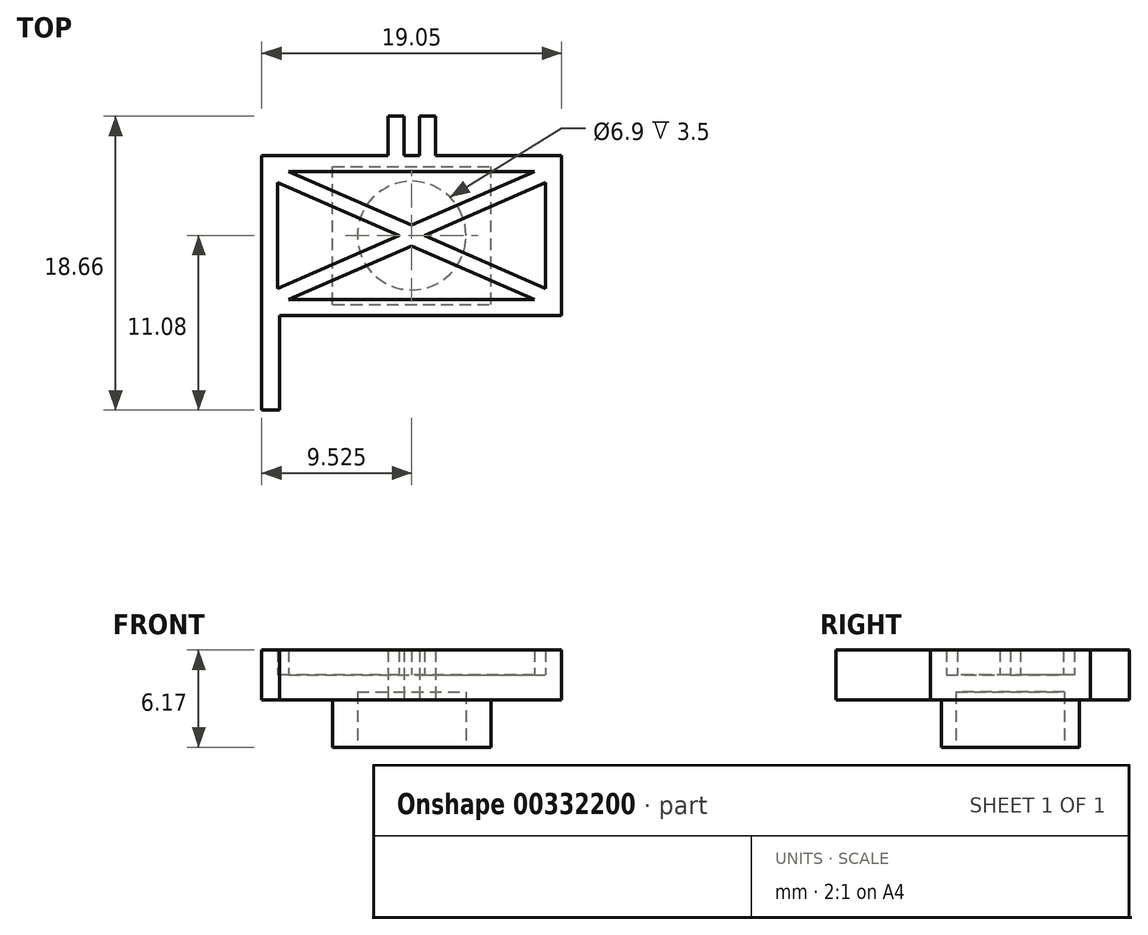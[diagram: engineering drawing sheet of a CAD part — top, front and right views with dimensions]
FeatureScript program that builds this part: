
annotation { "Feature Type Name" : "Feature", "Feature Type Description" : "" }
export const myFeature = defineFeature(function(context is Context, id is Id, definition is map)
    precondition{}
    {
        {
            var Q0;
            Q0=qCreatedBy(makeId("Top.planeOp"),FACE);
            var sketch = newSketch(context, id + "F0", { "sketchPlane" : qUnion([Q0])});
            skLineSegment(sketch, "E0.bottom", {"start": v(-19.05, 10.16) * mm, "end": v(0, 10.16) * mm});
            skLineSegment(sketch, "E0.top", {"start": v(-19.05, 0) * mm, "end": v(0, 0) * mm});
            skLineSegment(sketch, "E0.left", {"start": v(-19.05, 10.16) * mm, "end": v(-19.05, 0) * mm});
            skLineSegment(sketch, "E0.right", {"start": v(0, 10.16) * mm, "end": v(0, 0) * mm});
            skLineSegment(sketch, "E1", {"start": v(-9.52, 10.16) * mm, "end": v(-9.52, 0) * mm, "construction": true});
            skLineSegment(sketch, "E2.bottom", {"start": v(-9.02, 12.66) * mm, "end": v(-8.02, 12.66) * mm});
            skLineSegment(sketch, "E2.top", {"start": v(-9.02, 10.16) * mm, "end": v(-8.02, 10.16) * mm});
            skLineSegment(sketch, "E2.left", {"start": v(-9.02, 12.66) * mm, "end": v(-9.02, 10.16) * mm});
            skLineSegment(sketch, "E2.right", {"start": v(-8.02, 12.66) * mm, "end": v(-8.02, 10.16) * mm});
            skLineSegment(sketch, "E3.MirrorCS", {"start": v(-10.03, 12.66) * mm, "end": v(-10.03, 10.16) * mm});
            skLineSegment(sketch, "E4.MirrorCS", {"start": v(-11.03, 12.66) * mm, "end": v(-11.03, 10.16) * mm});
            skLineSegment(sketch, "E5.MirrorCS", {"start": v(-10.03, 12.66) * mm, "end": v(-11.03, 12.66) * mm});
            skSolve(sketch);
        }
        {
            var Q0;
            Q0=qSketchRegion(id+"F0",true);
            extrude(context, id + "F1", {"entities" : qUnion([Q0]), "depth" : 3.17 * mm});
        }
        {
            var Q0;
            Q0=makeQuery(id+"F1.opExtrude","CAP_FACE",FACE,{"disambiguationData":[OSD([sQuery(id+"F0.wireOp",EDGE,"E0.bottom"),sQuery(id+"F0.wireOp",EDGE,"E0.top"),sQuery(id+"F0.wireOp",EDGE,"E0.left"),sQuery(id+"F0.wireOp",EDGE,"E0.right")])],"isStart":false});
            var sketch = newSketch(context, id + "F2", { "sketchPlane" : qUnion([Q0])});
            skLineSegment(sketch, "E6.bottom", {"start": v(-18.03, 9.14) * mm, "end": v(-1.02, 9.14) * mm});
            skLineSegment(sketch, "E6.top", {"start": v(-18.03, 1.02) * mm, "end": v(-1.02, 1.02) * mm});
            skLineSegment(sketch, "E6.left", {"start": v(-18.03, 9.14) * mm, "end": v(-18.03, 1.02) * mm});
            skLineSegment(sketch, "E6.right", {"start": v(-1.02, 9.14) * mm, "end": v(-1.02, 1.02) * mm});
            skSolve(sketch);
        }
        {
            var Q0;
            Q0=qSketchRegion(id+"F2",true);
            extrude(context, id + "F3", {"entities" : qUnion([Q0]), "operationType" : NewBodyOperationType.REMOVE, "oppositeDirection" : true, "depth" : 1.59 * mm});
        }
        {
            var Q0;
            {var subQ1=sQuery(id+"F2.wireOp",EDGE,"E6.top");var subQ4=makeQuery(id+"F3.boolean.opBoolean","COPY",FACE,{"derivedFrom":makeQuery(id+"F3.opExtrude","SWEPT_FACE",FACE,{"disambiguationData":[OSD([subQ1])]})});var subQ6=sQuery(id+"F2.wireOp",EDGE,"E6.right");Q0=makeQuery(id+"FbiU5rRMadnEj1Y_1.boolean.opBoolean","SPLIT",FACE,{"disambiguationData":[TD([subQ4])],"derivedFrom":makeQuery(id+"FD6hazfNaiJcgqe_1.boolean.opBoolean","SPLIT",FACE,{"disambiguationData":[TD([subQ4])],"derivedFrom":makeQuery(id+"F3.boolean.opBoolean","COPY",FACE,{"derivedFrom":makeQuery(id+"F3.opExtrude","CAP_FACE",FACE,{"disambiguationData":[OSD([sQuery(id+"F2.wireOp",EDGE,"E6.bottom"),subQ1,sQuery(id+"F2.wireOp",EDGE,"E6.left"),subQ6])],"isStart":false})})})});}
            var sketch = newSketch(context, id + "F4", { "sketchPlane" : qUnion([Q0])});
            skLineSegment(sketch, "E7", {"start": v(-19.05, 1.68) * mm, "end": v(-1.02, 1.68) * mm, "construction": true});
            skLineSegment(sketch, "E8", {"start": v(-9.53, 10.16) * mm, "end": v(-9.53, 0) * mm, "construction": true});
            skSolve(sketch);
        }
        {
            var Q0;
            Q0=makeQuery(id+"F1.opExtrude","CAP_FACE",FACE,{"disambiguationData":[OSD([sQuery(id+"F0.wireOp",EDGE,"E0.bottom"),sQuery(id+"F0.wireOp",EDGE,"E0.top"),sQuery(id+"F0.wireOp",EDGE,"E0.left"),sQuery(id+"F0.wireOp",EDGE,"E0.right"),sQuery(id+"F0.wireOp",EDGE,"iD4YVwzi-38ZZ-sZow-cuPB-LK5aPxXRs2tg"),sQuery(id+"F0.wireOp",EDGE,"25aa8db4-dd9b-41d2-b8c9-1594e9b75191"),sQuery(id+"F0.wireOp",EDGE,"40f63cb3-13d8-4821-a3c4-c05e674bd89b0.MirrorC")])],"isStart":true});
            var sketch = newSketch(context, id + "F5", { "sketchPlane" : qUnion([Q0])});
            skLineSegment(sketch, "E9.bottom", {"start": v(-14.55, -0.7) * mm, "end": v(-4.5, -0.7) * mm});
            skLineSegment(sketch, "E9.top", {"start": v(-14.55, -9.46) * mm, "end": v(-4.5, -9.46) * mm});
            skLineSegment(sketch, "E9.left", {"start": v(-14.55, -0.7) * mm, "end": v(-14.55, -9.46) * mm});
            skLineSegment(sketch, "E9.right", {"start": v(-4.5, -0.7) * mm, "end": v(-4.5, -9.46) * mm});
            skSolve(sketch);
        }
        {
            var Q0;
            Q0=qSketchRegion(id+"F5",true);
            extrude(context, id + "F6", {"entities" : qUnion([Q0]), "operationType" : NewBodyOperationType.ADD, "depth" : 3 * mm, "offsetDistance" : 25 * mm});
        }
        {
            var Q0;
            Q0=makeQuery(id+"F6.opExtrude","CAP_FACE",FACE,{"disambiguationData":[OSD([sQuery(id+"F5.wireOp",EDGE,"E9.bottom"),sQuery(id+"F5.wireOp",EDGE,"E9.top"),sQuery(id+"F5.wireOp",EDGE,"E9.left"),sQuery(id+"F5.wireOp",EDGE,"E9.right")])],"isStart":false});
            var sketch = newSketch(context, id + "F7", { "sketchPlane" : qUnion([Q0])});
            skCircle(sketch, "E10", {"center": v(-9.52, -5.08) * mm, "radius": 3.45 * mm});
            skLineSegment(sketch, "E11", {"start": v(-19.05, -5.08) * mm, "end": v(0, -5.08) * mm, "construction": true});
            skPoint(sketch, "E11.endSnap0", {"position": v(-4.5, -5.08) * mm});
            skLineSegment(sketch, "E12", {"start": v(-9.53, 0) * mm, "end": v(-9.53, -9.46) * mm, "construction": true});
            skSolve(sketch);
        }
        {
            var Q0;
            Q0=makeQuery(id+"F7.imprint","IMPRINT",FACE,{"disambiguationData":[TD([[makeQuery(id+"F7.imprint","IMPRINT",EDGE,{"derivedFrom":sQuery(id+"F7.wireOp",EDGE,"E10")}),1.0]])]});
            extrude(context, id + "F8", {"entities" : qUnion([Q0]), "operationType" : NewBodyOperationType.REMOVE, "oppositeDirection" : true, "depth" : 3.5 * mm, "offsetDistance" : 25 * mm});
        }
        {
            var Q0;
            Q0=makeQuery(id+"F4.imprint","IMPRINT",FACE,{"disambiguationData":[TD([[makeQuery(id+"F4.imprint","IMPRINT",EDGE,{"derivedFrom":makeQuery(id+"F3.boolean.opBoolean","COPY",EDGE,{"derivedFrom":makeQuery(id+"F3.opExtrude","CAP_EDGE",EDGE,{"disambiguationData":[OSD([sQuery(id+"F2.wireOp",EDGE,"E6.bottom")])],"isStart":false})})}),-1.0]])]});
            var sketch = newSketch(context, id + "F9", { "sketchPlane" : qUnion([Q0])});
            skLineSegment(sketch, "E13", {"start": v(-1.72, 9.14) * mm, "end": v(-9.53, 5.74) * mm});
            skLineSegment(sketch, "E14", {"start": v(-8.73, 5.08) * mm, "end": v(-1.02, 8.44) * mm});
            skLineSegment(sketch, "E15", {"start": v(-1.02, 8.44) * mm, "end": v(-1.02, 9.14) * mm});
            skLineSegment(sketch, "E16", {"start": v(-1.02, 9.14) * mm, "end": v(-1.72, 9.14) * mm});
            skLineSegment(sketch, "E17", {"start": v(-19.05, 5.08) * mm, "end": v(0, 5.08) * mm, "construction": true});
            skLineSegment(sketch, "E18.MirrorCS", {"start": v(-17.33, 9.14) * mm, "end": v(-9.53, 5.74) * mm});
            skLineSegment(sketch, "E19.MirrorCS", {"start": v(-10.33, 5.08) * mm, "end": v(-18.03, 8.44) * mm});
            skLineSegment(sketch, "E20.MirrorCS", {"start": v(-18.03, 8.44) * mm, "end": v(-18.03, 9.14) * mm});
            skLineSegment(sketch, "E21.MirrorCS", {"start": v(-18.03, 9.14) * mm, "end": v(-17.33, 9.14) * mm});
            skLineSegment(sketch, "E22.MirrorCS", {"start": v(-10.33, 5.08) * mm, "end": v(-18.03, 1.72) * mm});
            skLineSegment(sketch, "E23.MirrorCS", {"start": v(-8.73, 5.08) * mm, "end": v(-1.02, 1.72) * mm});
            skLineSegment(sketch, "E24.MirrorCS", {"start": v(-1.72, 1.02) * mm, "end": v(-9.53, 4.42) * mm});
            skLineSegment(sketch, "E25.MirrorCS", {"start": v(-17.33, 1.02) * mm, "end": v(-9.53, 4.42) * mm});
            skLineSegment(sketch, "E26.MirrorCS", {"start": v(-18.03, 1.02) * mm, "end": v(-17.33, 1.02) * mm});
            skLineSegment(sketch, "E27.MirrorCS", {"start": v(-18.03, 1.72) * mm, "end": v(-18.03, 1.02) * mm});
            skLineSegment(sketch, "E28.MirrorCS", {"start": v(-1.02, 1.72) * mm, "end": v(-1.02, 1.02) * mm});
            skLineSegment(sketch, "E29.MirrorCS", {"start": v(-1.02, 1.02) * mm, "end": v(-1.72, 1.02) * mm});
            skSolve(sketch);
        }
        {
            var Q0;
            Q0=qSketchRegion(id+"F9",true);
            var Q1;
            Q1=makeQuery(id+"FXsS83p9KQ4uv0L_1.boolean.opBoolean","MERGE",FACE,{"derivedFrom":[makeQuery(id+"F1.opExtrude","CAP_FACE",FACE,{"disambiguationData":[OSD([sQuery(id+"F0.wireOp",EDGE,"E0.bottom"),sQuery(id+"F0.wireOp",EDGE,"E0.top"),sQuery(id+"F0.wireOp",EDGE,"E0.left"),sQuery(id+"F0.wireOp",EDGE,"E0.right"),sQuery(id+"F0.wireOp",EDGE,"25aa8db4-dd9b-41d2-b8c9-1594e9b75191"),sQuery(id+"F0.wireOp",EDGE,"40f63cb3-13d8-4821-a3c4-c05e674bd89b0.MirrorC")])],"isStart":false}),makeQuery(id+"FbiU5rRMadnEj1Y_1.opExtrude","CAP_FACE",FACE,{"disambiguationData":[OSD([sQuery(id+"FmV1InaubWQgJeV_1.wireOp",EDGE,"lTleeF4S-0pnc-dI25-KJAR-2TLCTf0jWGc3"),sQuery(id+"FmV1InaubWQgJeV_1.wireOp",EDGE,"m9JDErra-axgF-Q1Zk-CJc0-x6RwavRCbCz8")])],"isStart":false}),makeQuery(id+"FXsS83p9KQ4uv0L_1.opExtrude","CAP_FACE",FACE,{"disambiguationData":[OSD([sQuery(id+"Fi3yzKCDt9pSW51_1.wireOp",EDGE,"cutzoVbR-JFbv-1kZ0-SQrw-pSLFGMZcN76v"),sQuery(id+"Fi3yzKCDt9pSW51_1.wireOp",EDGE,"XYQyWRLz-35l4-wHee-0FsY-Oat0KQk3jhR6"),sQuery(id+"Fi3yzKCDt9pSW51_1.wireOp",EDGE,"lBgadLLx-aQS8-kMAZ-d5qN-Zo8duSUxtBeX"),sQuery(id+"Fi3yzKCDt9pSW51_1.wireOp",EDGE,"DlRPRQGx-Alaq-SPUL-URFH-jddu6C2Nnp9z"),sQuery(id+"Fi3yzKCDt9pSW51_1.wireOp",EDGE,"Shc4e2eY-gIsf-lYKj-D0sO-212MCfLGw1w2"),sQuery(id+"Fi3yzKCDt9pSW51_1.wireOp",EDGE,"DXv1RSob-CDWK-uPmN-nh2c-bdjhB3yjVnB2"),sQuery(id+"Fi3yzKCDt9pSW51_1.wireOp",EDGE,"Mjf90MPI-7UZW-OfA1-fD3l-TGEU1IJ1uaYu"),sQuery(id+"Fi3yzKCDt9pSW51_1.wireOp",EDGE,"IrneLFi4-a4Xm-RgwH-oJvY-WcCPALNDAReP"),sQuery(id+"Fi3yzKCDt9pSW51_1.wireOp",EDGE,"toQdHavX-h7D1-dxbV-IXrh-P84p4AImceJh"),sQuery(id+"Fi3yzKCDt9pSW51_1.wireOp",EDGE,"xGw8HYbu-oKFY-4S3u-lNNy-w4TfAhwJFqQu"),sQuery(id+"Fi3yzKCDt9pSW51_1.wireOp",EDGE,"5pvZd2gl-M8UA-9HNZ-daD7-4TEjzgTyMgsA"),sQuery(id+"Fi3yzKCDt9pSW51_1.wireOp",EDGE,"b1702624-0c59-4015-bc2e-a5f6b81265a70.MirrorCS"),sQuery(id+"Fi3yzKCDt9pSW51_1.wireOp",EDGE,"7deeccc9-7886-4666-b44c-47b900ed28990.MirrorCS"),sQuery(id+"Fi3yzKCDt9pSW51_1.wireOp",EDGE,"75936777-967d-44d6-aacf-753113c8b50b0.MirrorCS"),sQuery(id+"Fi3yzKCDt9pSW51_1.wireOp",EDGE,"e5875930-5b2f-47d0-b261-f87a419dd3ea0.MirrorCS"),sQuery(id+"Fi3yzKCDt9pSW51_1.wireOp",EDGE,"e1f8200d-9078-41b5-85b4-8a4adb8dc9e80.MirrorCS"),sQuery(id+"Fi3yzKCDt9pSW51_1.wireOp",EDGE,"40fd4d9e-f758-4b42-b7b5-3e08d0cf58f50.MirrorCS"),sQuery(id+"Fi3yzKCDt9pSW51_1.wireOp",EDGE,"553d3a6c-e9a7-4b40-b1d3-0817f640e5cc0.MirrorCS"),sQuery(id+"Fi3yzKCDt9pSW51_1.wireOp",EDGE,"5a723a2c-c48e-43ea-a32e-a11b15ff1a7b0.MirrorCS"),sQuery(id+"Fi3yzKCDt9pSW51_1.wireOp",EDGE,"932d58c0-4b54-410d-a467-0e9cf49887c90.MirrorCS"),sQuery(id+"Fi3yzKCDt9pSW51_1.wireOp",EDGE,"eeedfdb4-aa26-4e83-bf33-b18388155c4d0.MirrorCS"),sQuery(id+"Fi3yzKCDt9pSW51_1.wireOp",EDGE,"a4c71cba-da55-4cc9-80cf-8947727491d80.MirrorCS")])],"isStart":false})]});
            extrude(context, id + "F10", {"entities" : qUnion([Q0]), "operationType" : NewBodyOperationType.ADD, "endBound" : BoundingType.UP_TO_SURFACE, "depth" : 25 * mm, "endBoundEntityFace" : qUnion([Q1]), "offsetDistance" : 25 * mm});
        }
        {
            var Q0;
            Q0=makeQuery(id+"F1.opExtrude","SWEPT_FACE",FACE,{"disambiguationData":[OSD([sQuery(id+"F0.wireOp",EDGE,"E0.top")])]});
            var sketch = newSketch(context, id + "F11", { "sketchPlane" : qUnion([Q0])});
            skLineSegment(sketch, "E30.bottom", {"start": v(-19.05, 3.18) * mm, "end": v(-17.9, 3.18) * mm});
            skLineSegment(sketch, "E30.top", {"start": v(-19.05, 0) * mm, "end": v(-17.9, 0) * mm});
            skLineSegment(sketch, "E30.left", {"start": v(-19.05, 3.18) * mm, "end": v(-19.05, 0) * mm});
            skLineSegment(sketch, "E30.right", {"start": v(-17.9, 3.18) * mm, "end": v(-17.9, 0) * mm});
            skSolve(sketch);
        }
        {
            var Q0;
            Q0=qSketchRegion(id+"F11",true);
            extrude(context, id + "F12", {"entities" : qUnion([Q0]), "operationType" : NewBodyOperationType.ADD, "depth" : 6 * mm, "offsetDistance" : 25 * mm});
        }
    });
